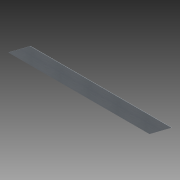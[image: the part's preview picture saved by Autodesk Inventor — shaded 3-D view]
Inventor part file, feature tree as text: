
AUTODESK INVENTOR PART (.ipt)
format: ipt  version: 2011 SP1 (Build 150282100, 282)  size: 70,656 bytes
history: native  units: in
note: dims shown in document units (in); Inventor stores cm internally (conversion verified against a paired STEP export)
features: extrude x1, sketch x1
ambient origin geometry x8: Origin, YZ Plane, XZ Plane, XY Plane, X Axis, Y Axis, Z Axis, Center Point
bodies: Solid1 (feature_tree)
feature tree (2):
  extrude  "Extrusion1"  Depth=3.0in
  sketch  "Sketch1"  dims[d0=25.7218in d1=3.0in d2=4.0in d3=0.0625in d4=0.0in]
